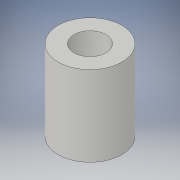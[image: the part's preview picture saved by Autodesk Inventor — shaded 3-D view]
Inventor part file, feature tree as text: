
AUTODESK INVENTOR PART (.ipt)
format: ipt  version: 2019.4 (Build 234330000, 330)  size: 100,352 bytes
history: native  units: in
note: dims shown in document units (in); Inventor stores cm internally (conversion verified against a paired STEP export)
features: extrude x2, sketch x2
ambient origin geometry x8: Origin, YZ Plane, XZ Plane, XY Plane, X Axis, Y Axis, Z Axis, Center Point
bodies: Solid1 (feature_tree)
feature tree (4):
  extrude  "Extrusion1"  Depth=0.315in TaperAngle=0.0deg
  extrude  "Extrusion2"  Depth=0.315in TaperAngle=0.0deg
  sketch  "Sketch1"  dims[d0=0.25in d1=0.315in d2=0.0in]
  sketch  "Sketch2"  dims[d3=0.125in d4=0.315in d5=0.0in]
